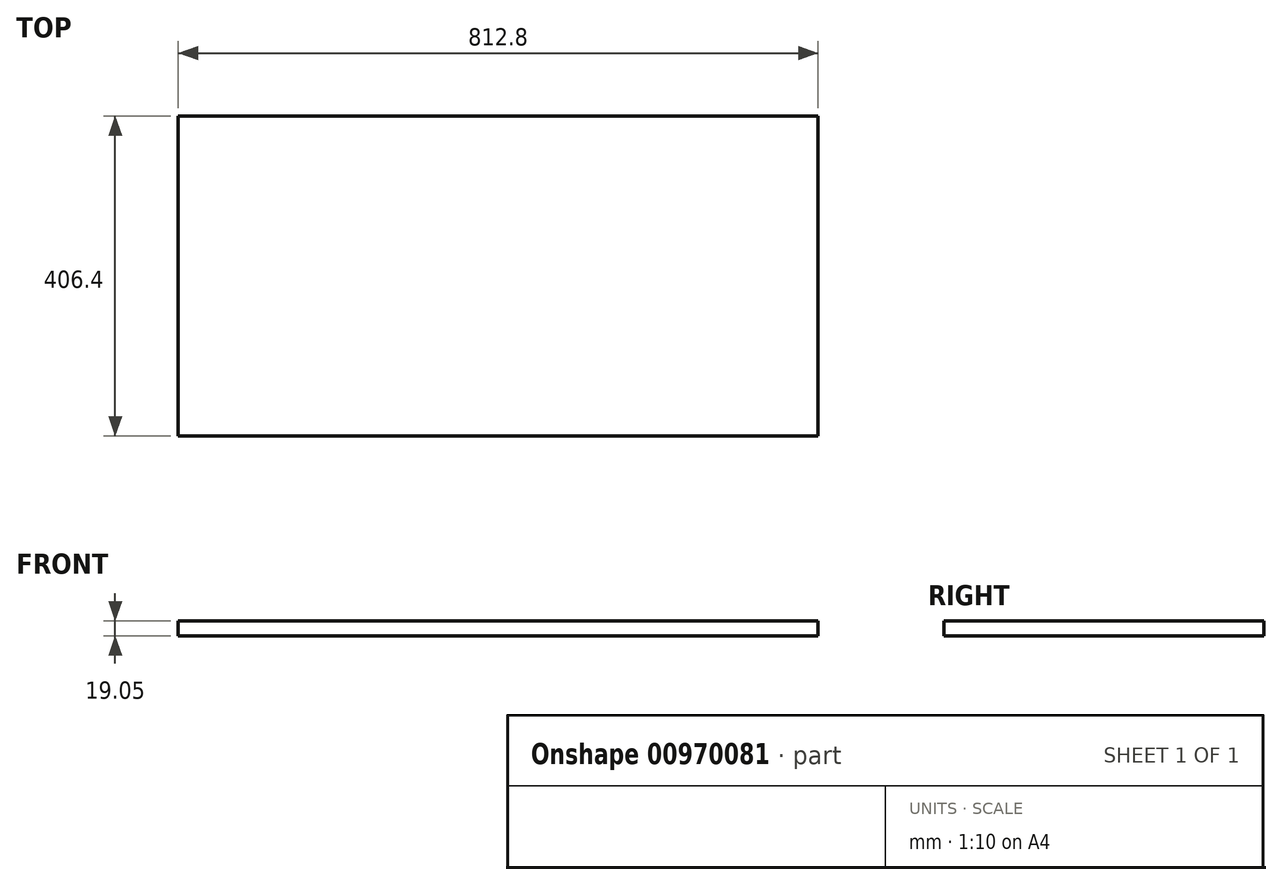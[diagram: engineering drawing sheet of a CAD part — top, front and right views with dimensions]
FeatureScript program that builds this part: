
annotation { "Feature Type Name" : "Feature", "Feature Type Description" : "" }
export const myFeature = defineFeature(function(context is Context, id is Id, definition is map)
    precondition{}
    {
        {
            var Q0;
            Q0=qCreatedBy(makeId("Top.planeOp"),FACE);
            var sketch = newSketch(context, id + "F0", { "sketchPlane" : qUnion([Q0])});
            skLineSegment(sketch, "E0.bottom", {"start": v(0, 0) * mm, "end": v(812.8, 0) * mm});
            skLineSegment(sketch, "E0.top", {"start": v(0, 406.4) * mm, "end": v(812.8, 406.4) * mm});
            skLineSegment(sketch, "E0.left", {"start": v(0, 0) * mm, "end": v(0, 406.4) * mm});
            skLineSegment(sketch, "E0.right", {"start": v(812.8, 0) * mm, "end": v(812.8, 406.4) * mm});
            skSolve(sketch);
        }
        {
            var Q0;
            Q0=makeQuery(id+"F0.imprint","IMPRINT",FACE,{"disambiguationData":[TD([[makeQuery(id+"F0.imprint","IMPRINT",EDGE,{"derivedFrom":sQuery(id+"F0.wireOp",EDGE,"E0.bottom")}),1.0]])]});
            extrude(context, id + "F1", {"entities" : qUnion([Q0]), "depth" : 19.05 * mm, "offsetDistance" : 25.4 * mm});
        }
    });
